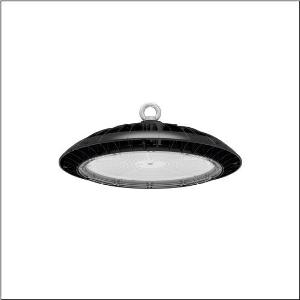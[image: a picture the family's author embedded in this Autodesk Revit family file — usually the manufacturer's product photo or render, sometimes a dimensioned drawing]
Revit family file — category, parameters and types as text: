
# Revit family: highbay_42-l_51hp32mb4mma
name_source: partatom
category: Lighting Fixtures
units: mm (PartAtom-declared; Revit-internal decimal feet)

## family parameters
Cut with Voids When Loaded = No
Host = Face
Light Source = No
Part Type = Normal
Room Calculation Point = No
Round Connector Dimension = Use Diameter
Shared = No

## types (1)
- --- (1 x LED, 28000 lm, 175 W, 4000K)
    Apparent Load = 175 VA
    CIE Flux Codes = 49 82 98 100 100
    Color Rendering = 80
    Color Temperature = 4000K
    Default Elevation = 1800 mm
    Description = Highbay 42-L, LED high bay luminaire, primary light control with lens, of PC, primary optical cover: cover panel, of PC, transparent, light emission: direct distribution, primary light characteristic: rotationally symmetric, installation type: suspended mounting, surface-mounted, LED, rated luminous flux: 28.000lm, luminous efficacy: 160lm/W, light colour: 840, colour temperature: 4000K, control gear: ECG, with cable, 3x 1.0mm², free wire ends, mains connection: 230V, AC, 50Hz, cable length: 1,5m, rated input power: 175W, housing, rotationally symmetric, of diecast aluminium, black, with hook on luminaire side, diameter: 305mm, height: 117mm, protection rating (complete): IP65, insulation class (complete): insulation class I (protective earthing), certification: CE, UKCA, protection symbol: D, impact resistance: IK08, permissible operating ambient temperature: -20..+40°C, corresponds to IFS (International Featured Standards) requirements for safety and quality in the food industry, packaging unit: 1 piece
    Height = 117 mm
    Lamp = 1 x LED
    Lamp Light Flux = 28000 lm
    Lamp Power = 175 W
    Lamp count = 1
    Length = 305 mm
    Luminous efficacy = 160 lm/W
    Manufacturer = Siteco
    ModVariant = No
    Model = 51HP32MB4MMA
    Mounting Place = Ceiling
    Mounting Type = Pendant
    Number of Poles = 1
    OnlyDefault = Yes
    Power Factor = 1
    Product Name = Highbay 42-L
    Product group = LED high bay luminaire
    ProductGroupID = 903
    Protection Class = Protection class I
    Protection Degree = IP 65
    RLX_Detail_Level = 1
    RLX_Emergency_Light_Flux = 0 lm
    RLX_Emergency_Type = 0
    RLX_Emergency_Type_DB = No
    RlxData = <blob elided: 286777 chars, md5=fbeda471>
    Socket = socket
    Standby Power = 0 W
    System Light Flux = 28000 lm
    System Power = 175 W
    Type Comments = factory setting: luminous flux: 100 % | (OFF | OFF | OFF)
    Type Image = l_1003932.jpg
    URL = http://relux.com
    VarID = @adj_135331
    Voltage = 0 V
    Weight = 0.00 kg
    Width = 0 mm  [stored 0 ft]

note: [stored X ft] marks values corroborated as IEEE doubles in the binary element streams (Revit-internal decimal feet)

## geometry (parser evidence)
native form markers: Blend x4, Sweep x11
no freeform markers — native parametric forms only
